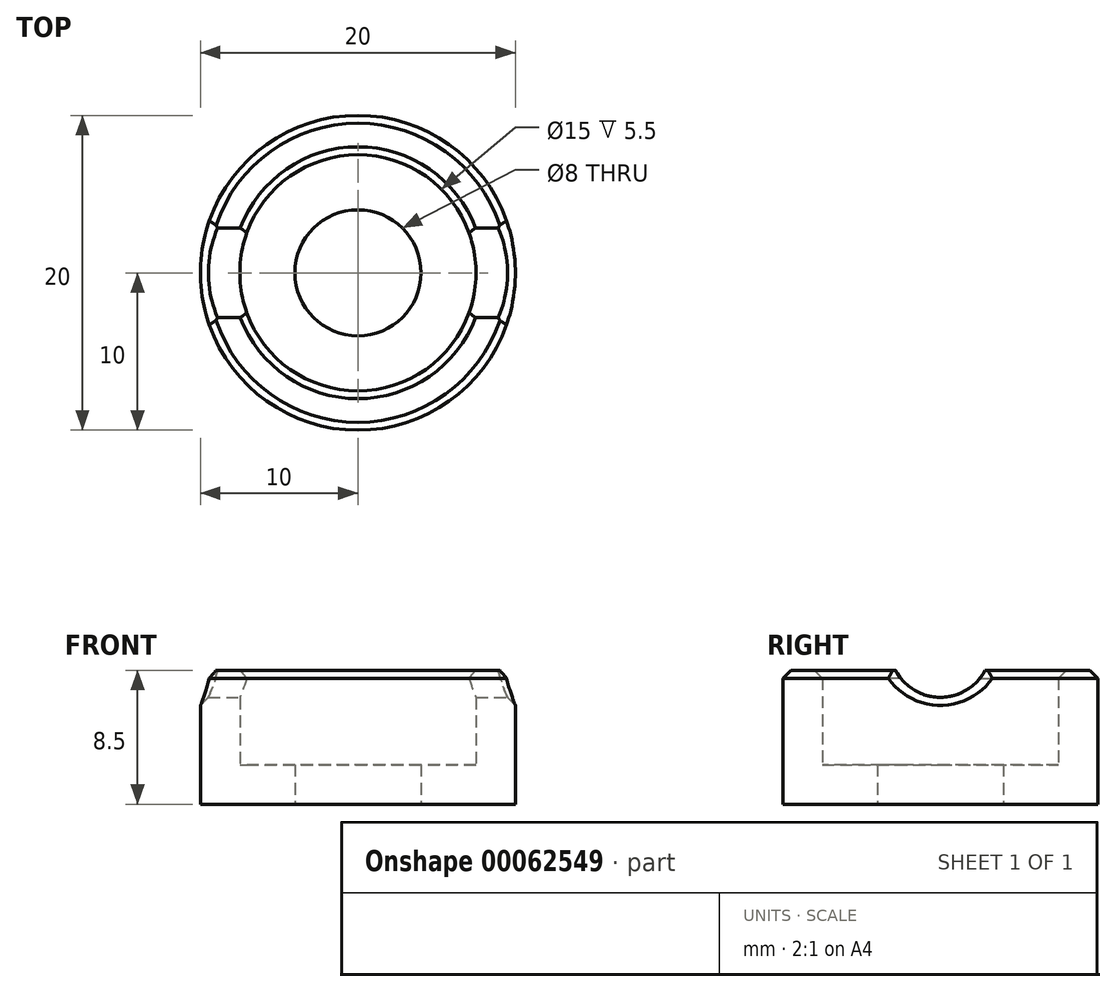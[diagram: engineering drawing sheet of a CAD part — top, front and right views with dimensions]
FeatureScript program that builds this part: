
annotation { "Feature Type Name" : "Feature", "Feature Type Description" : "" }
export const myFeature = defineFeature(function(context is Context, id is Id, definition is map)
    precondition{}
    {
        {
            var Q0;
            Q0=qCreatedBy(makeId("Top.planeOp"),FACE);
            var sketch = newSketch(context, id + "F0", { "sketchPlane" : qUnion([Q0])});
            skCircle(sketch, "E0", {"center": v(0, 0) * mm, "radius": 10 * mm});
            skCircle(sketch, "E1.0", {"center": v(0, 0) * mm, "radius": 7.5 * mm});
            skCircle(sketch, "E2.0", {"center": v(0, 0) * mm, "radius": 4 * mm});
            skSolve(sketch);
        }
        {
            var Q0;
            Q0=makeQuery(id+"F0.imprint","IMPRINT",FACE,{"disambiguationData":[TD([[makeQuery(id+"F0.imprint","IMPRINT",EDGE,{"derivedFrom":sQuery(id+"F0.wireOp",EDGE,"E0")}),1.0]])]});
            extrude(context, id + "F1", {"entities" : qUnion([Q0]), "depth" : 8.5 * mm});
        }
        {
            var Q0;
            Q0=makeQuery(id+"F0.imprint","IMPRINT",FACE,{"disambiguationData":[TD([[makeQuery(id+"F0.imprint","IMPRINT",EDGE,{"derivedFrom":sQuery(id+"F0.wireOp",EDGE,"E1.0")}),1.0]])]});
            extrude(context, id + "F2", {"entities" : qUnion([Q0]), "operationType" : NewBodyOperationType.ADD, "depth" : 2.5 * mm});
        }
        {
            var Q0;
            Q0=qCreatedBy(makeId("Right.planeOp"),FACE);
            var sketch = newSketch(context, id + "F3", { "sketchPlane" : qUnion([Q0])});
            skCircle(sketch, "E3", {"center": v(0, 10) * mm, "radius": 3.22 * mm});
            skLineSegment(sketch, "E4", {"start": v(0, 0) * mm, "end": v(0, 10) * mm});
            skLineSegment(sketch, "E5", {"start": v(0, 0) * mm, "end": v(-15.25, 0) * mm});
            skSolve(sketch);
        }
        {
            var Q0;
            Q0=makeQuery(id+"F3.imprint","IMPRINT",FACE,{"disambiguationData":[TD([[makeQuery(id+"F3.imprint","IMPRINT",EDGE,{"derivedFrom":sQuery(id+"F3.wireOp",EDGE,"E3")}),1.0]])]});
            extrude(context, id + "F4", {"entities" : qUnion([Q0]), "operationType" : NewBodyOperationType.REMOVE, "endBound" : BoundingType.SYMMETRIC, "oppositeDirection" : true, "depth" : 25 * mm});
        }
        {
            var Q0;
            Q0=makeQuery(id+"F4.boolean.opBoolean","SPLIT",EDGE,{"disambiguationData":[OD(1.0)],"derivedFrom":makeQuery(id+"F1.opExtrude","CAP_EDGE",EDGE,{"disambiguationData":[OSD([sQuery(id+"F0.wireOp",EDGE,"E0")])],"isStart":false})});
            var Q1;
            Q1=makeQuery(id+"F4.boolean.opBoolean","SPLIT",EDGE,{"disambiguationData":[OD(0.0)],"derivedFrom":makeQuery(id+"F1.opExtrude","CAP_EDGE",EDGE,{"disambiguationData":[OSD([sQuery(id+"F0.wireOp",EDGE,"E0")])],"isStart":false})});
            var Q2;
            Q2=makeQuery(id+"F4.boolean.opBoolean","SPLIT",EDGE,{"disambiguationData":[OD(0.0)],"derivedFrom":makeQuery(id+"F1.opExtrude","CAP_EDGE",EDGE,{"disambiguationData":[OSD([sQuery(id+"F0.wireOp",EDGE,"E1.0")])],"isStart":false})});
            var Q3;
            Q3=makeQuery(id+"F4.boolean.opBoolean","SPLIT",EDGE,{"disambiguationData":[OD(1.0)],"derivedFrom":makeQuery(id+"F1.opExtrude","CAP_EDGE",EDGE,{"disambiguationData":[OSD([sQuery(id+"F0.wireOp",EDGE,"E1.0")])],"isStart":false})});
            chamfer(context, id + "F5", {"entities" : qUnion([Q0, Q1, Q2, Q3]), "width" : 0.5 * mm, "tangentPropagation" : true});
        }
        {
            var Q0;
            Q0=makeQuery(id+"F4.boolean.opBoolean","INTERSECT",EDGE,{"disambiguationData":[OD(1.0)],"derivedFrom":[makeQuery(id+"F1.opExtrude","SWEPT_FACE",FACE,{"disambiguationData":[OSD([sQuery(id+"F0.wireOp",EDGE,"E0")])]}),makeQuery(id+"F4.opExtrude","SWEPT_FACE",FACE,{"disambiguationData":[OSD([sQuery(id+"F3.wireOp",EDGE,"E3")])]})]});
            var Q1;
            Q1=makeQuery(id+"F4.boolean.opBoolean","INTERSECT",EDGE,{"disambiguationData":[OD(0.0)],"derivedFrom":[makeQuery(id+"F1.opExtrude","SWEPT_FACE",FACE,{"disambiguationData":[OSD([sQuery(id+"F0.wireOp",EDGE,"E0")])]}),makeQuery(id+"F4.opExtrude","SWEPT_FACE",FACE,{"disambiguationData":[OSD([sQuery(id+"F3.wireOp",EDGE,"E3")])]})]});
            chamfer(context, id + "F6", {"entities" : qUnion([Q0, Q1]), "width" : 0.5 * mm, "tangentPropagation" : true});
        }
    });
